# Revit family: S-771
name_source: partatom
category: Plumbing Fixtures
revit_build: Autodesk Revit 2015 (Build: 20140606_1530(x64)
units: mm (PartAtom-declared; Revit-internal decimal feet)

## types (6) — shared parameters
Description = SHOWER CHANNEL FOR TILED SHOWERS, ORIENTABLE TRAP, ORIENTABLE HORIZONTAL OUTLET, WITH GRID CLASSIC, WITH HEIGHT REGULATION FEET
Emax = 16 mm  [stored 0.0524934 ft]
Emin = 6 mm  [stored 0.019685 ft]
Flowrate = 0.8 L/s
Grid = INOX AISI304
H_Diameter = 40 mm  [stored 0.131234 ft]
Hidraulic seal = 50 mm
Manufacturer = Jimten
Material = ABS
Model = S-771
Outlet = 40M/50M
Total Minimum Height = 121-131 mm
Type Comments = WITH PRESSING RING FOR WATERPROOFING PVC OR GEOTEXTILE MEMBRANES. WITH PROTECTION COVER.  WITH GRID HEIGHT ADJUSTABLE.
URL = http://www.jimten.com
WFU = 1

## per-type parameters (varying)
| type | A_Outlet | B_Grid | DistLegs | Reference | Size | Type Grid |
| 70x650mm_Classic | 700 mm  [stored 2.29659 ft] | 670 mm  [stored 2.19816 ft] | 500 mm  [stored 1.64042 ft] | 13716 | 650mm x 70mm | 10 |
| 70x750mm_Classic | 800 mm  [stored 2.62467 ft] | 770 mm  [stored 2.52625 ft] | 600 mm | 13717 | 750mm x 70mm | 11 |
| 70x850mm_Classic | 900 mm  [stored 2.95276 ft] | 870 mm  [stored 2.85433 ft] | 700 mm  [stored 2.29659 ft] | 13718 | 850mm x 70mm | 13 |
| 70x950mm_Classic | 1000 mm  [stored 3.28084 ft] | 970 mm  [stored 3.18241 ft] | 800 mm  [stored 2.62467 ft] | 13719 | 950mm x 70mm | 14 |
| 70x350mm_Classic | 400 mm  [stored 1.31234 ft] | 370 mm  [stored 1.21391 ft] | 300 mm | 13713 | 350mm x 70mm | 5 |
| 70x550mm_Classic | 600 mm | 570 mm  [stored 1.87008 ft] | 400 mm  [stored 1.31234 ft] | 13715 | 550mm x 70mm | 8 |

note: [stored X ft] marks values corroborated as IEEE doubles in the binary element streams (Revit-internal decimal feet)

## geometry (parser evidence)
native form markers: Blend x3, Sweep x10
no freeform markers — native parametric forms only
